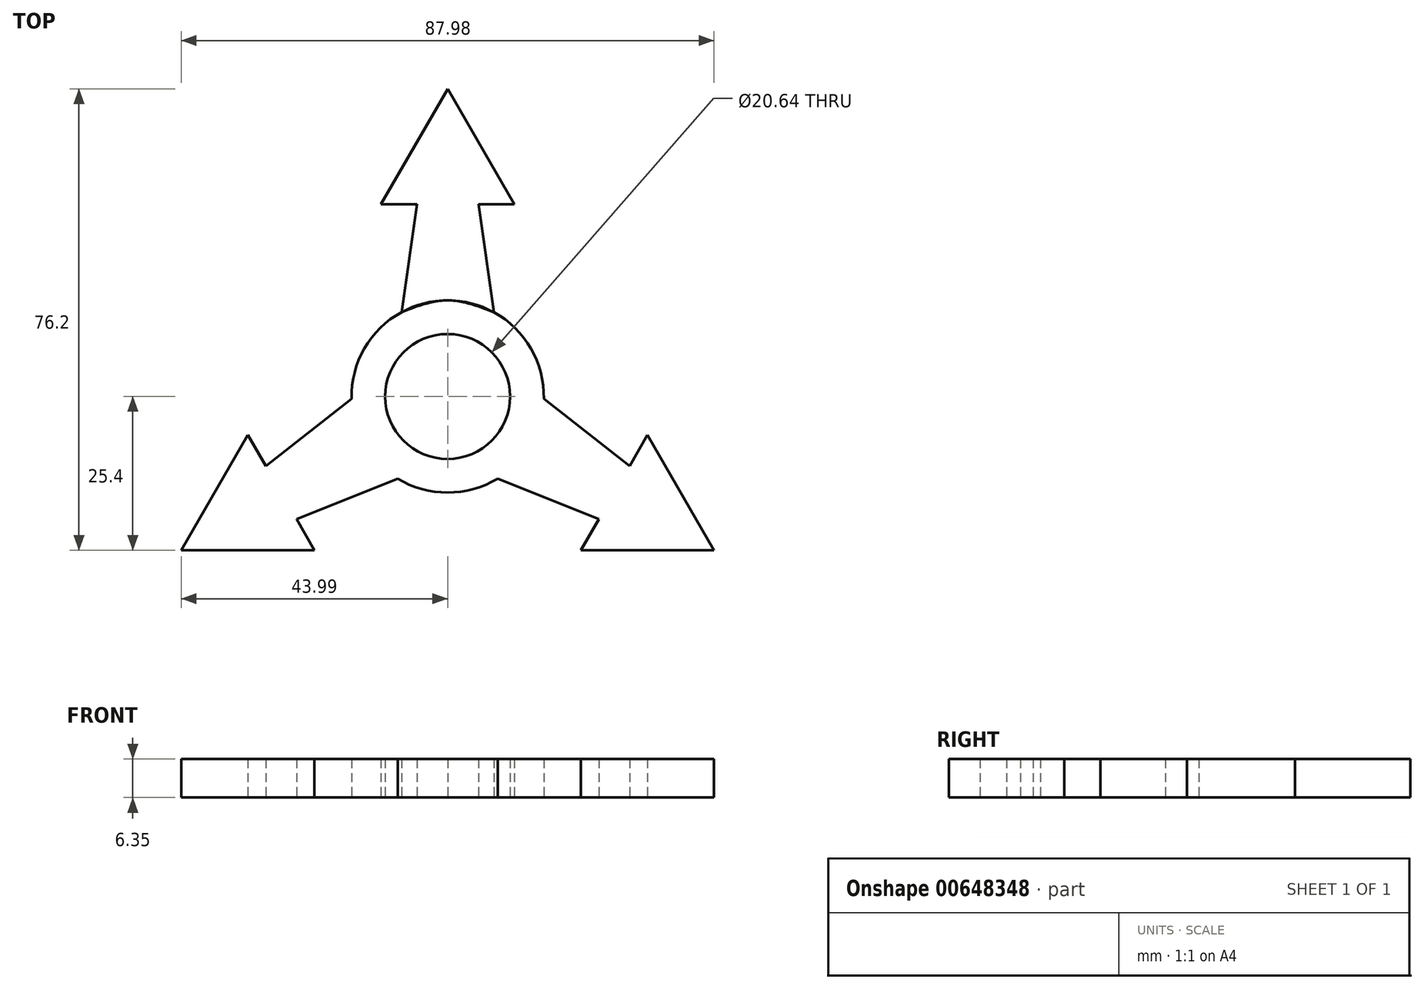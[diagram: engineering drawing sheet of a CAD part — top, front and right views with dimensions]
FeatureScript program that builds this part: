
annotation { "Feature Type Name" : "Feature", "Feature Type Description" : "" }
export const myFeature = defineFeature(function(context is Context, id is Id, definition is map)
    precondition{}
    {
        {
            var Q0;
            Q0=qCreatedBy(makeId("Top.planeOp"),FACE);
            var sketch = newSketch(context, id + "F0", { "sketchPlane" : qUnion([Q0])});
            skCircle(sketch, "E0", {"center": v(0, 0) * mm, "radius": 15.88 * mm});
            skCircle(sketch, "E1", {"center": v(0, 0) * mm, "radius": 10.32 * mm});
            skLineSegment(sketch, "E2.0", {"start": v(0, 50.8) * mm, "end": v(11, 31.75) * mm});
            skLineSegment(sketch, "E2.1", {"start": v(11, 31.75) * mm, "end": v(-11, 31.75) * mm});
            skLineSegment(sketch, "E2.2", {"start": v(-11, 31.75) * mm, "end": v(0, 50.8) * mm});
            skLineSegment(sketch, "E3", {"start": v(-5.08, 31.75) * mm, "end": v(-7.62, 13.93) * mm});
            skLineSegment(sketch, "E4", {"start": v(5.08, 31.75) * mm, "end": v(7.62, 13.93) * mm});
            skFitSpline(sketch, "E5", {"points": [v(-7.62, 13.93) * mm, v(0, 15.88) * mm, v(7.62, 13.93) * mm], "startDerivative": vector(15.24, 5.85) * mm, "endDerivative": vector(15.24, -5.85) * mm});
            skLineSegment(sketch, "E6", {"start": v(-5.08, 31.75) * mm, "end": v(5.08, 31.75) * mm});
            skLineSegment(sketch, "E7.1.0", {"start": v(-30.04, -11.48) * mm, "end": v(-15.87, -0.36) * mm});
            skLineSegment(sketch, "E7.1.1", {"start": v(-24.96, -20.27) * mm, "end": v(-30.04, -11.48) * mm});
            skLineSegment(sketch, "E7.1.2", {"start": v(-24.96, -20.27) * mm, "end": v(-8.25, -13.56) * mm});
            skLineSegment(sketch, "E7.1.3", {"start": v(-22, -25.4) * mm, "end": v(-44, -25.4) * mm});
            skLineSegment(sketch, "E7.1.4", {"start": v(-44, -25.4) * mm, "end": v(-33, -6.35) * mm});
            skLineSegment(sketch, "E7.1.5", {"start": v(-33, -6.35) * mm, "end": v(-22, -25.4) * mm});
            skLineSegment(sketch, "E7.2.0", {"start": v(24.96, -20.27) * mm, "end": v(8.25, -13.56) * mm});
            skLineSegment(sketch, "E7.2.1", {"start": v(30.04, -11.48) * mm, "end": v(24.96, -20.27) * mm});
            skLineSegment(sketch, "E7.2.2", {"start": v(30.04, -11.48) * mm, "end": v(15.87, -0.36) * mm});
            skLineSegment(sketch, "E7.2.3", {"start": v(33, -6.35) * mm, "end": v(44, -25.4) * mm});
            skLineSegment(sketch, "E7.2.4", {"start": v(44, -25.4) * mm, "end": v(22, -25.4) * mm});
            skLineSegment(sketch, "E7.2.5", {"start": v(22, -25.4) * mm, "end": v(33, -6.35) * mm});
            skSolve(sketch);
        }
        {
            var Q0;
            {var subQ1=sQuery(id+"F0.wireOp",EDGE,"E3");Q0=makeQuery(id+"F0.imprint","IMPRINT",FACE,{"disambiguationData":[TD([[makeQuery(id+"F0.imprint","IMPRINT",EDGE,{"derivedFrom":subQ1}),1.0]])]});}
            var Q1;
            Q1=makeQuery(id+"F0.imprint","IMPRINT",FACE,{"disambiguationData":[TD([[makeQuery(id+"F0.imprint","IMPRINT",EDGE,{"derivedFrom":sQuery(id+"F0.wireOp",EDGE,"E1")}),-1.0]])]});
            var Q2;
            {var subQ0=sQuery(id+"F0.wireOp",EDGE,"E7.1.0");Q2=makeQuery(id+"F0.imprint","IMPRINT",FACE,{"disambiguationData":[TD([[makeQuery(id+"F0.imprint","IMPRINT",EDGE,{"derivedFrom":subQ0}),-1.0]])]});}
            var Q3;
            {var subQ4=sQuery(id+"F0.wireOp",EDGE,"E7.1.3");Q3=makeQuery(id+"F0.imprint","IMPRINT",FACE,{"disambiguationData":[TD([[makeQuery(id+"F0.imprint","IMPRINT",EDGE,{"derivedFrom":subQ4}),-1.0]])]});}
            var Q4;
            {var subQ0=sQuery(id+"F0.wireOp",EDGE,"E7.2.0");Q4=makeQuery(id+"F0.imprint","IMPRINT",FACE,{"disambiguationData":[TD([[makeQuery(id+"F0.imprint","IMPRINT",EDGE,{"derivedFrom":subQ0}),-1.0]])]});}
            var Q5;
            {var subQ4=sQuery(id+"F0.wireOp",EDGE,"E7.2.3");Q5=makeQuery(id+"F0.imprint","IMPRINT",FACE,{"disambiguationData":[TD([[makeQuery(id+"F0.imprint","IMPRINT",EDGE,{"derivedFrom":subQ4}),-1.0]])]});}
            var Q6;
            {var subQ3=sQuery(id+"F0.wireOp",EDGE,"E2.0");Q6=makeQuery(id+"F0.imprint","IMPRINT",FACE,{"disambiguationData":[TD([[makeQuery(id+"F0.imprint","IMPRINT",EDGE,{"derivedFrom":subQ3}),-1.0]])]});}
            extrude(context, id + "F1", {"entities" : qUnion([Q0, Q1, Q2, Q3, Q4, Q5, Q6]), "depth" : 6.35 * mm, "offsetDistance" : 25.4 * mm});
        }
    });
